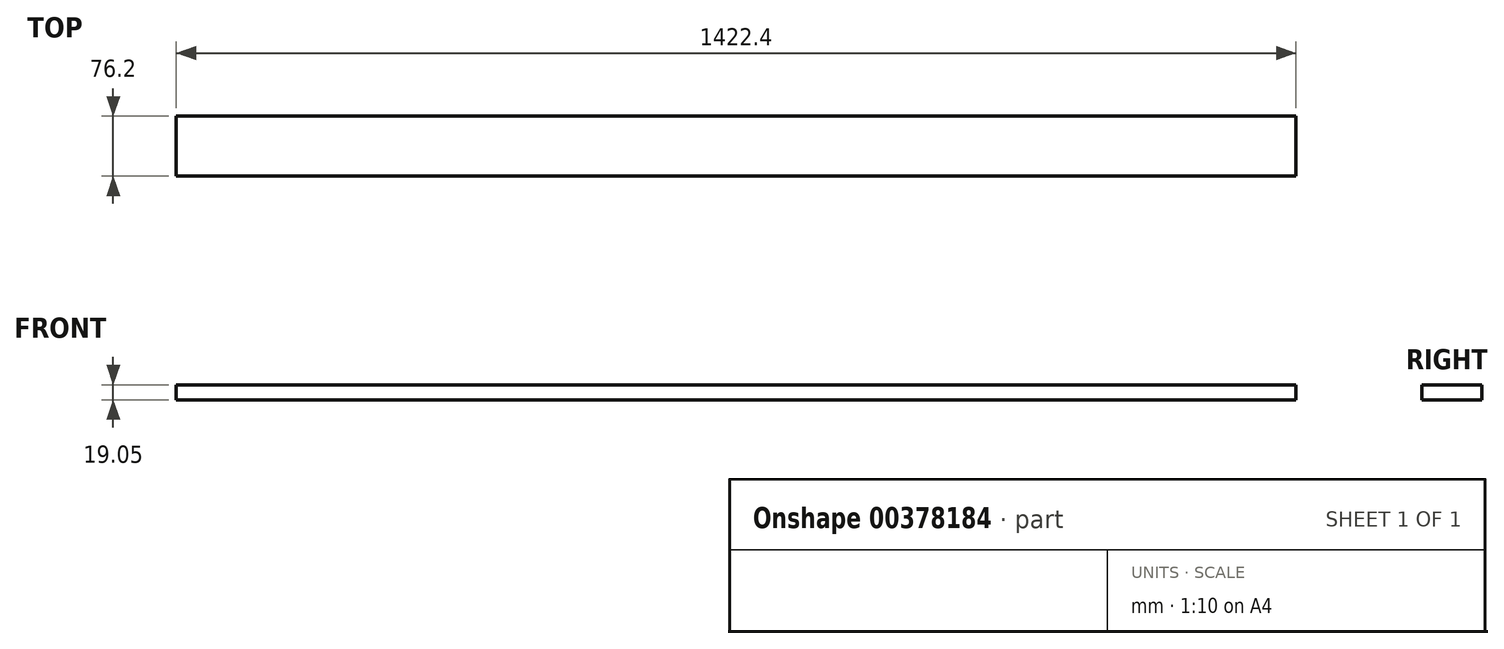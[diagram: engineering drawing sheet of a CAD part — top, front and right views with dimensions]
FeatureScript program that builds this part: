
annotation { "Feature Type Name" : "Feature", "Feature Type Description" : "" }
export const myFeature = defineFeature(function(context is Context, id is Id, definition is map)
    precondition{}
    {
        {
            var Q0;
            Q0=qCreatedBy(makeId("Top.planeOp"),FACE);
            var sketch = newSketch(context, id + "F0", { "sketchPlane" : qUnion([Q0])});
            skLineSegment(sketch, "E0.bottom", {"start": v(0, 0) * mm, "end": v(1422.4, 0) * mm});
            skLineSegment(sketch, "E0.top", {"start": v(0, -76.2) * mm, "end": v(1422.4, -76.2) * mm});
            skLineSegment(sketch, "E0.left", {"start": v(0, 0) * mm, "end": v(0, -76.2) * mm});
            skLineSegment(sketch, "E0.right", {"start": v(1422.4, 0) * mm, "end": v(1422.4, -76.2) * mm});
            skSolve(sketch);
        }
        {
            var Q0;
            Q0=makeQuery(id+"F0.imprint","IMPRINT",FACE,{"disambiguationData":[TD([[makeQuery(id+"F0.imprint","IMPRINT",EDGE,{"derivedFrom":sQuery(id+"F0.wireOp",EDGE,"E0.bottom")}),-1.0]])]});
            extrude(context, id + "F1", {"entities" : qUnion([Q0]), "depth" : 19.05 * mm});
        }
    });
